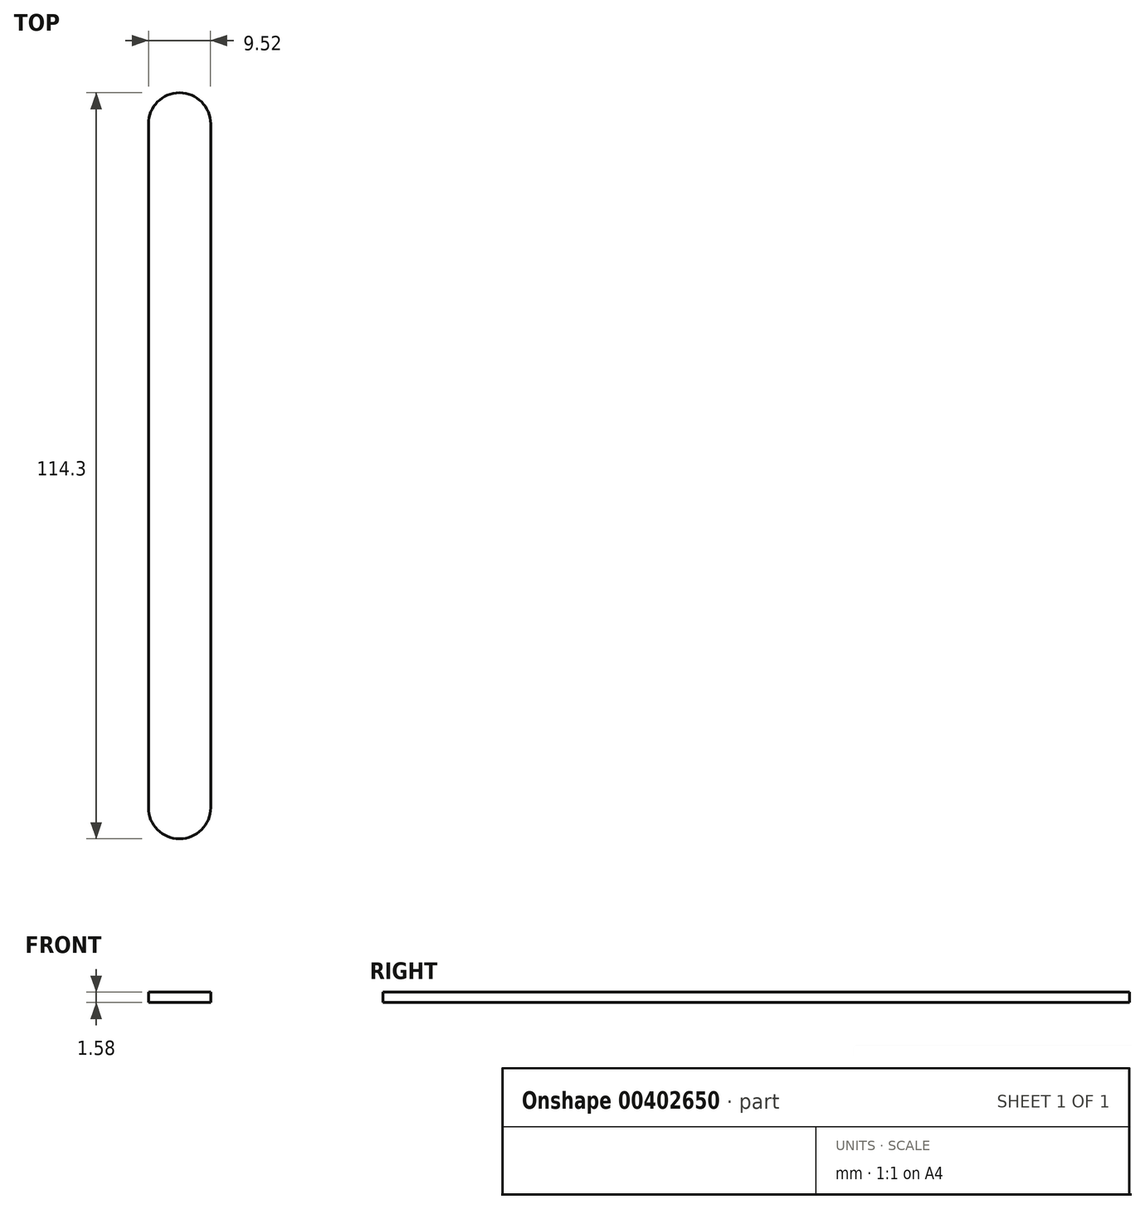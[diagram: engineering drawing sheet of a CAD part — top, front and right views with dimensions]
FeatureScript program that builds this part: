
annotation { "Feature Type Name" : "Feature", "Feature Type Description" : "" }
export const myFeature = defineFeature(function(context is Context, id is Id, definition is map)
    precondition{}
    {
        {
            var Q0;
            Q0=qCreatedBy(makeId("Top.planeOp"),FACE);
            var sketch = newSketch(context, id + "F0", { "sketchPlane" : qUnion([Q0])});
            skLineSegment(sketch, "E0.bottom", {"start": v(4.76, -52.39) * mm, "end": v(-4.76, -52.39) * mm});
            skLineSegment(sketch, "E0.top", {"start": v(4.76, 52.39) * mm, "end": v(-4.76, 52.39) * mm});
            skLineSegment(sketch, "E0.left", {"start": v(4.76, -52.39) * mm, "end": v(4.76, 52.39) * mm});
            skLineSegment(sketch, "E0.right", {"start": v(-4.76, -52.39) * mm, "end": v(-4.76, 52.39) * mm});
            skPoint(sketch, "E0.middle", {"position": v(0, 0) * mm});
            skArc(sketch, "E1", {"start": v(-4.76, 52.39) * mm, "mid": v(0, 57.15) * mm, "end": v(4.76, 52.39) * mm});
            skArc(sketch, "E2", {"start": v(-4.76, -52.39) * mm, "mid": v(0, -57.15) * mm, "end": v(4.76, -52.39) * mm});
            skSolve(sketch);
        }
        {
            var Q0;
            Q0 = qSketchRegion(id + "F0", true);
            extrude(context, id + "F1", {"entities" : qUnion([Q0]), "depth" : 1.59 * mm, "symmetric" : true});
        }
    });
